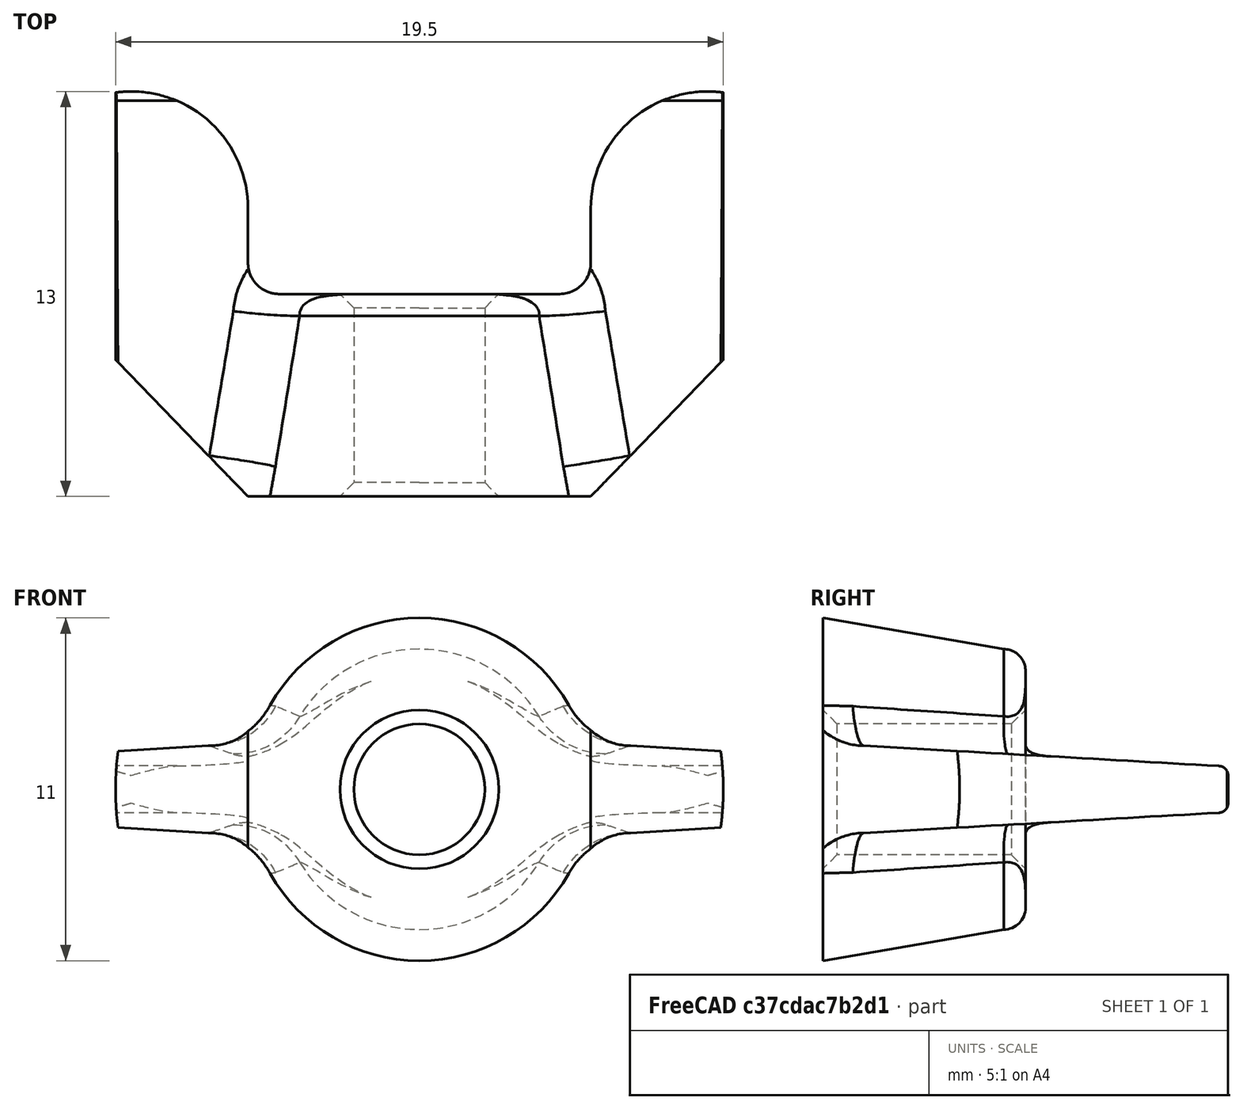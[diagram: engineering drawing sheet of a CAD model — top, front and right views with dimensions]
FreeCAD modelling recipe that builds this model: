
FCSTD DOCUMENT  (FreeCAD 0.19R24267 +99 (Git))
Label: Assembly M5 wing nut trimmed wings
License: All rights reserved
LicenseURL: http://en.wikipedia.org/wiki/All_rights_reserved
objects: Part::Feature×1, Sketcher::SketchObject×1, PartDesign::Pad×1, PartDesign::Body×1, Part::Cut×1
note: 6 computed .brp shape members not serialized (recipe doc carries the construction recipe); baked Part::Feature solids carry a one-line shape summary decoded from their .brp

FEATURE [Part::Feature] Part__Feature  label="TR Fastenings Ltd-M5"
  shape: bbox 26.31 x 13.15 x 11 mm, 45 faces (baked)
FEATURE [Sketcher::SketchObject] Sketch
  FullyConstrained = true
  MapMode = 5
  Placement = pos=(0,0,0) rot=(1,0,0;1.5708rad)
  Support = -> [XZ_Plane]
  sketch-geometry (2):
    g0: Circle CenterX=0 CenterY=0 CenterZ=0 NormalX=0 NormalY=0 NormalZ=1 AngleXU=0 Radius=9.75
    g1: Circle CenterX=0 CenterY=0 CenterZ=0 NormalX=0 NormalY=0 NormalZ=1 AngleXU=0 Radius=15
  constraints (4):
    c: Coincident(g0,g-1)
    c: Coincident(g1,g0)
    c: Diameter(g0) = 19.5
    c: Diameter(g1) = 30
FEATURE [PartDesign::Pad] Pad
  Direction = (1,1,1)
  Length = 25
  Length2 = 100
  Placement = pos=(0,0,0) rot=(1,0,0;1.5708rad)
  Profile = -> Sketch
  Reversed = true
  Type = 0
FEATURE [PartDesign::Body] Body
  Group = -> [Sketch,Pad]
  Origin = -> Origin
  Tip = -> Pad
FEATURE [Part::Cut] Cut
  Base = -> Part__Feature
  Tool = -> Body
